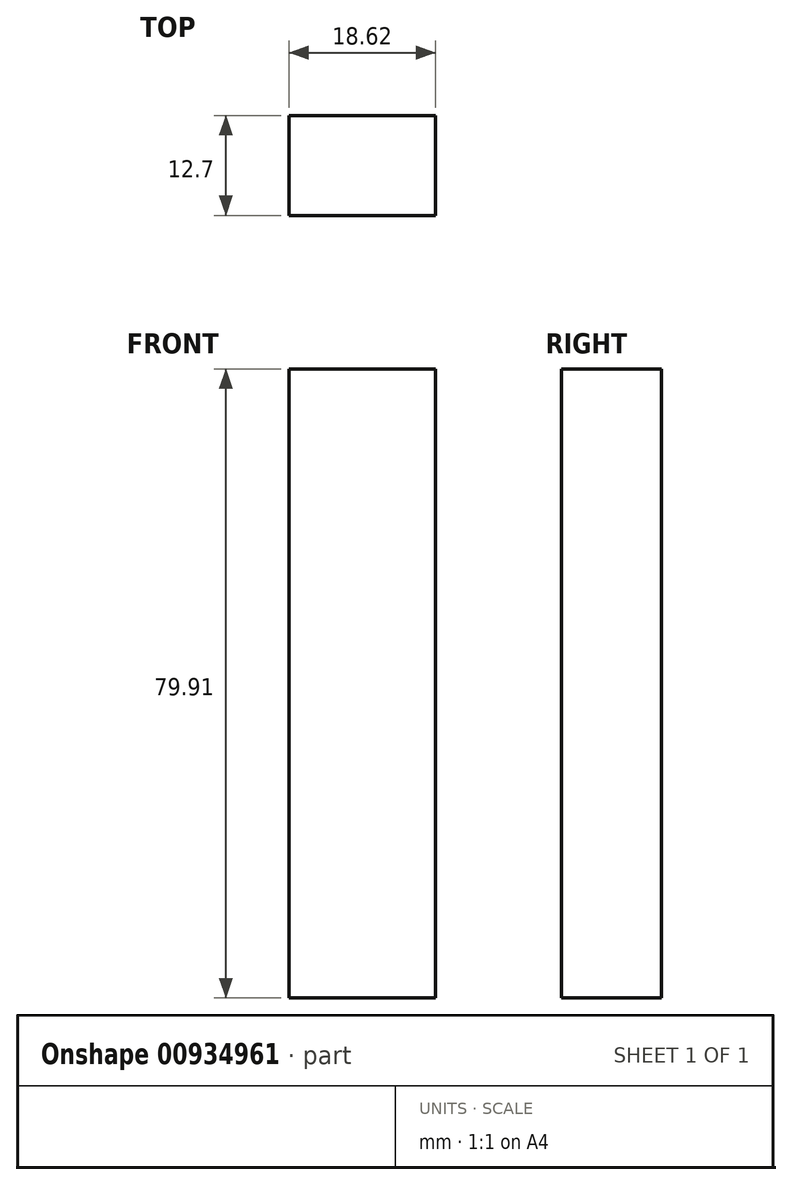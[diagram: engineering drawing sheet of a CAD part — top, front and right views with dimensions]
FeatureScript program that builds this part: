
annotation { "Feature Type Name" : "Feature", "Feature Type Description" : "" }
export const myFeature = defineFeature(function(context is Context, id is Id, definition is map)
    precondition{}
    {
        {
            var Q0;
            Q0=qCreatedBy(makeId("Front.planeOp"),FACE);
            var sketch = newSketch(context, id + "F0", { "sketchPlane" : qUnion([Q0])});
            skLineSegment(sketch, "E0.bottom", {"start": v(-29.68, -55.08) * mm, "end": v(29.68, -55.08) * mm});
            skLineSegment(sketch, "E0.top", {"start": v(-29.68, 55.08) * mm, "end": v(29.68, 55.08) * mm});
            skLineSegment(sketch, "E0.left", {"start": v(-29.68, -55.08) * mm, "end": v(-29.68, 55.08) * mm});
            skLineSegment(sketch, "E0.right", {"start": v(29.68, -55.08) * mm, "end": v(29.68, 55.08) * mm});
            skPoint(sketch, "E0.middle", {"position": v(0, 0) * mm});
            skLineSegment(sketch, "E1.bottom", {"start": v(-18.81, -98.52) * mm, "end": v(18.81, -98.52) * mm});
            skLineSegment(sketch, "E1.top", {"start": v(-18.81, -55.07) * mm, "end": v(18.81, -55.07) * mm});
            skLineSegment(sketch, "E1.left", {"start": v(-18.81, -98.52) * mm, "end": v(-18.81, -55.07) * mm});
            skLineSegment(sketch, "E1.right", {"start": v(18.81, -98.52) * mm, "end": v(18.81, -55.07) * mm});
            skPoint(sketch, "E1.middle", {"position": v(0, -76.8) * mm});
            skLineSegment(sketch, "E2.bottom", {"start": v(-11.83, 84.57) * mm, "end": v(11.83, 84.57) * mm});
            skLineSegment(sketch, "E2.top", {"start": v(-11.83, 55.08) * mm, "end": v(11.83, 55.08) * mm});
            skLineSegment(sketch, "E2.left", {"start": v(-11.83, 84.57) * mm, "end": v(-11.83, 55.08) * mm});
            skLineSegment(sketch, "E2.right", {"start": v(11.83, 84.57) * mm, "end": v(11.83, 55.08) * mm});
            skPoint(sketch, "E2.middle", {"position": v(0, 69.82) * mm});
            skPoint(sketch, "E2.middle.positionSnap0", {"position": v(0, 55.08) * mm});
            skPoint(sketch, "E2.centerSnap0", {"position": v(0, 55.08) * mm});
            skLineSegment(sketch, "E3.bottom", {"start": v(-29.68, 55.08) * mm, "end": v(-48.3, 55.08) * mm});
            skLineSegment(sketch, "E3.top", {"start": v(-29.68, -24.83) * mm, "end": v(-48.3, -24.83) * mm});
            skLineSegment(sketch, "E3.left", {"start": v(-29.68, 55.08) * mm, "end": v(-29.68, -24.83) * mm});
            skLineSegment(sketch, "E3.right", {"start": v(-48.3, 55.08) * mm, "end": v(-48.3, -24.83) * mm});
            skLineSegment(sketch, "E4.bottom", {"start": v(29.68, 55.08) * mm, "end": v(50.23, 55.08) * mm});
            skLineSegment(sketch, "E4.top", {"start": v(29.68, -24.83) * mm, "end": v(50.23, -24.83) * mm});
            skLineSegment(sketch, "E4.left", {"start": v(29.68, 55.08) * mm, "end": v(29.68, -24.83) * mm});
            skLineSegment(sketch, "E4.right", {"start": v(50.23, 55.08) * mm, "end": v(50.23, -24.83) * mm});
            skSolve(sketch);
        }
        {
            var Q0;
            Q0=makeQuery(id+"F0.imprint","IMPRINT",FACE,{"disambiguationData":[TD([[makeQuery(id+"F0.imprint","IMPRINT",EDGE,{"derivedFrom":sQuery(id+"F0.wireOp",EDGE,"E3.bottom")}),1.0]])]});
            extrude(context, id + "F1", {"entities" : qUnion([Q0]), "endBound" : BoundingType.SYMMETRIC, "depth" : 12.7 * mm, "offsetDistance" : 25.4 * mm});
        }
    });
